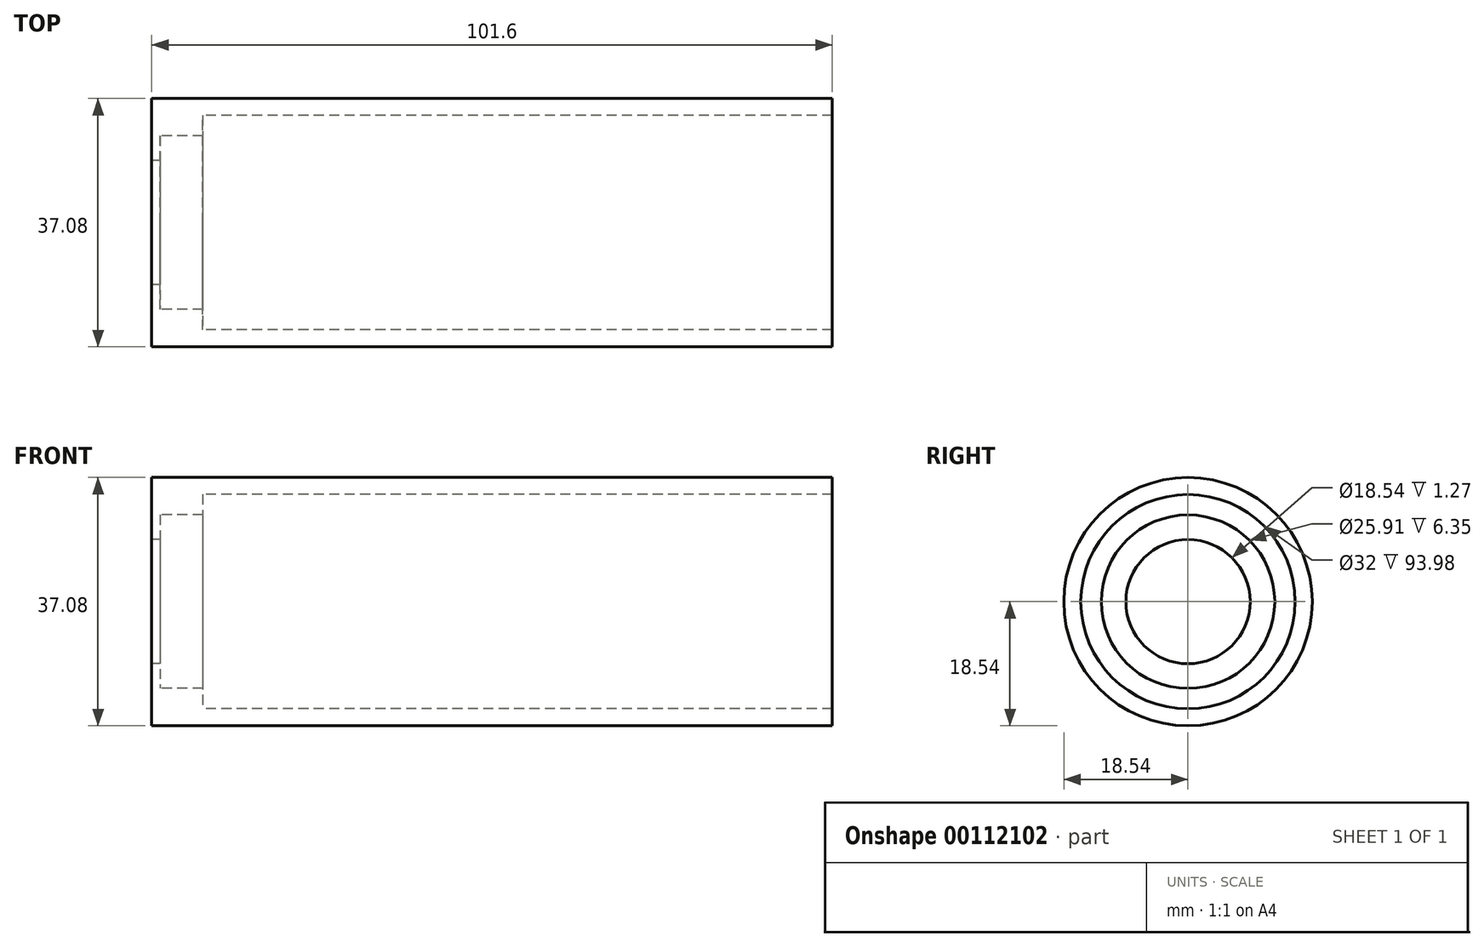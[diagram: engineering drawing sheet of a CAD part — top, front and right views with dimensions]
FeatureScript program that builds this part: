
annotation { "Feature Type Name" : "Feature", "Feature Type Description" : "" }
export const myFeature = defineFeature(function(context is Context, id is Id, definition is map)
    precondition{}
    {
        {
            var Q0;
            Q0=qCreatedBy(makeId("Front.planeOp"),FACE);
            var sketch = newSketch(context, id + "F0", { "sketchPlane" : qUnion([Q0])});
            skLineSegment(sketch, "E0", {"start": v(-73.66, 0) * mm, "end": v(46.42, 0) * mm, "construction": true});
            skLineSegment(sketch, "E1", {"start": v(-50.2, 9.27) * mm, "end": v(-50.2, 18.54) * mm});
            skLineSegment(sketch, "E2", {"start": v(-50.2, 18.54) * mm, "end": v(51.4, 18.54) * mm});
            skLineSegment(sketch, "E3", {"start": v(51.4, 18.54) * mm, "end": v(51.4, 16) * mm});
            skLineSegment(sketch, "E4", {"start": v(51.4, 16) * mm, "end": v(-42.58, 16) * mm});
            skLineSegment(sketch, "E5", {"start": v(-42.58, 16) * mm, "end": v(-42.58, 12.95) * mm});
            skLineSegment(sketch, "E6", {"start": v(-42.58, 12.95) * mm, "end": v(-48.93, 12.95) * mm});
            skLineSegment(sketch, "E7", {"start": v(-48.93, 12.95) * mm, "end": v(-48.93, 9.27) * mm});
            skLineSegment(sketch, "E8", {"start": v(-48.93, 0) * mm, "end": v(-50.2, 0) * mm});
            skLineSegment(sketch, "E9", {"start": v(-50.2, 9.27) * mm, "end": v(-48.93, 9.27) * mm});
            skSolve(sketch);
        }
        {
            var Q0;
            Q0=makeQuery(id+"F0.imprint","IMPRINT",FACE,{"disambiguationData":[TD([[makeQuery(id+"F0.imprint","IMPRINT",EDGE,{"derivedFrom":sQuery(id+"F0.wireOp",EDGE,"E1")}),-1.0]])]});
            var Q1;
            Q1=sQuery(id+"F0.wireOp",EDGE,"E0");
            revolve(context, id + "F1", {"entities" : qUnion([Q0]), "axis" : qUnion([Q1]), "revolveType" : RevolveType.FULL});
        }
    });
